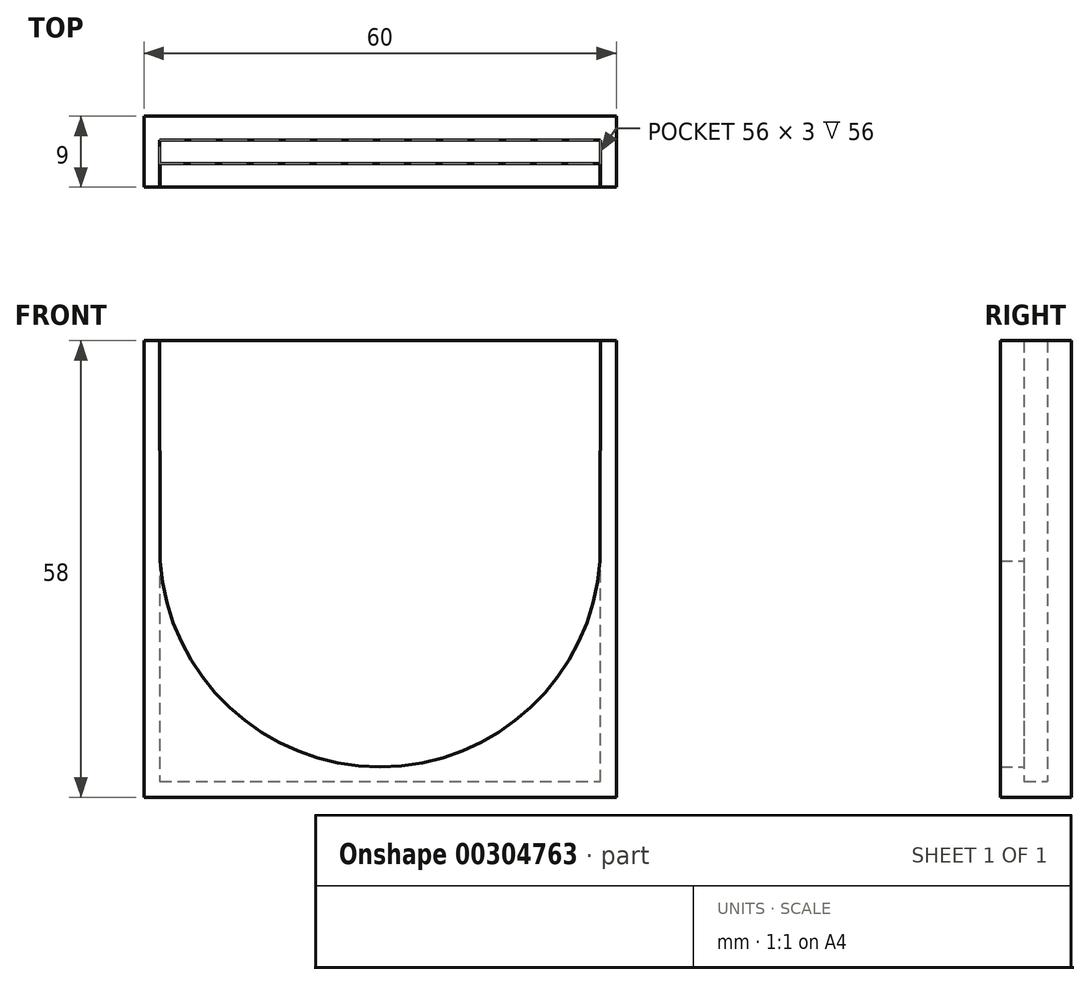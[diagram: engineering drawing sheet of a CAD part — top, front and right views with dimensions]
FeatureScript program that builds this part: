
annotation { "Feature Type Name" : "Feature", "Feature Type Description" : "" }
export const myFeature = defineFeature(function(context is Context, id is Id, definition is map)
    precondition{}
    {
        {
            var Q0;
            Q0=qCreatedBy(makeId("Front.planeOp"),FACE);
            var sketch = newSketch(context, id + "F0", { "sketchPlane" : qUnion([Q0])});
            skLineSegment(sketch, "E0.bottom", {"start": v(30, -30) * mm, "end": v(-30, -30) * mm});
            skLineSegment(sketch, "E0.top", {"start": v(30, 30) * mm, "end": v(-30, 30) * mm});
            skLineSegment(sketch, "E0.left", {"start": v(30, -30) * mm, "end": v(30, 30) * mm});
            skLineSegment(sketch, "E0.right", {"start": v(-30, -30) * mm, "end": v(-30, 30) * mm});
            skPoint(sketch, "E0.middle", {"position": v(0, 0) * mm});
            skLineSegment(sketch, "E1", {"start": v(-30, 28) * mm, "end": v(30, 28) * mm});
            skSolve(sketch);
        }
        {
            var Q0;
            Q0=makeQuery(id+"F0.imprint","IMPRINT",FACE,{"disambiguationData":[TD([[makeQuery(id+"F0.imprint","IMPRINT",EDGE,{"derivedFrom":sQuery(id+"F0.wireOp",EDGE,"E0.bottom")}),-1.0]])]});
            extrude(context, id + "F1", {"entities" : qUnion([Q0]), "oppositeDirection" : true, "depth" : 3 * mm});
        }
        {
            var Q0;
            Q0=makeQuery(id+"F1.opExtrude","CAP_FACE",FACE,{"disambiguationData":[OSD([sQuery(id+"F0.wireOp",EDGE,"E0.bottom"),sQuery(id+"F0.wireOp",EDGE,"E0.top"),sQuery(id+"F0.wireOp",EDGE,"E0.left"),sQuery(id+"F0.wireOp",EDGE,"E0.right")])],"isStart":true});
            var sketch = newSketch(context, id + "F2", { "sketchPlane" : qUnion([Q0])});
            skSolve(sketch);
        }
        {
            var Q0;
            Q0=makeQuery(id+"F2.imprint","IMPRINT",FACE,{"disambiguationData":[TD([[makeQuery(id+"F2.imprint","IMPRINT",EDGE,{"derivedFrom":makeQuery(id+"F1.opExtrude","CAP_EDGE",EDGE,{"disambiguationData":[OSD([sQuery(id+"F0.wireOp",EDGE,"E0.bottom")])],"isStart":true})}),-1.0]])]});
            var sketch = newSketch(context, id + "F3", { "sketchPlane" : qUnion([Q0])});
            skLineSegment(sketch, "E2.0", {"start": v(-28, -28) * mm, "end": v(28, -28) * mm});
            skLineSegment(sketch, "E2.1", {"start": v(-28, 28) * mm, "end": v(-28, -28) * mm});
            skLineSegment(sketch, "E2.3", {"start": v(28, -28) * mm, "end": v(28, 28) * mm});
            skLineSegment(sketch, "E3", {"start": v(-28, 28) * mm, "end": v(-30, 28) * mm});
            skLineSegment(sketch, "E4", {"start": v(-30, 28) * mm, "end": v(-30, -30) * mm});
            skLineSegment(sketch, "E5", {"start": v(-30, -30) * mm, "end": v(30, -30) * mm});
            skLineSegment(sketch, "E6", {"start": v(30, -30) * mm, "end": v(30, 28) * mm});
            skLineSegment(sketch, "E7", {"start": v(30, 28) * mm, "end": v(28, 28) * mm});
            skSolve(sketch);
        }
        {
            var Q0;
            Q0 = qSketchRegion(id + "F3", true);
            extrude(context, id + "F4", {"entities" : qUnion([Q0]), "operationType" : NewBodyOperationType.ADD, "depth" : 3 * mm});
        }
        {
            var Q0;
            Q0=makeQuery(id+"F4.opExtrude","CAP_FACE",FACE,{"disambiguationData":[OSD([sQuery(id+"F3.wireOp",EDGE,"E2.0"),sQuery(id+"F3.wireOp",EDGE,"E2.1"),sQuery(id+"F3.wireOp",EDGE,"E2.3"),sQuery(id+"F3.wireOp",EDGE,"E3"),sQuery(id+"F3.wireOp",EDGE,"E4"),sQuery(id+"F3.wireOp",EDGE,"E5"),sQuery(id+"F3.wireOp",EDGE,"E6"),sQuery(id+"F3.wireOp",EDGE,"E7")])],"isStart":false});
            var sketch = newSketch(context, id + "F5", { "sketchPlane" : qUnion([Q0])});
            skLineSegment(sketch, "E8.bottom", {"start": v(-30, -30) * mm, "end": v(30, -30) * mm});
            skLineSegment(sketch, "E8.top", {"start": v(-30, 28) * mm, "end": v(-28, 28) * mm});
            skLineSegment(sketch, "E8.left", {"start": v(-30, -30) * mm, "end": v(-30, 28) * mm});
            skLineSegment(sketch, "E8.right", {"start": v(30, -30) * mm, "end": v(30, 28) * mm});
            skArc(sketch, "E9", {"start": v(-27.95, 3.6) * mm, "mid": v(0, -26.14) * mm, "end": v(27.95, 3.6) * mm});
            skLineSegment(sketch, "E10", {"start": v(28, 28) * mm, "end": v(27.94, 0) * mm});
            skLineSegment(sketch, "E11", {"start": v(-28, 28) * mm, "end": v(-27.94, 0) * mm});
            skLineSegment(sketch, "E12.trimOffspring", {"start": v(28, 28) * mm, "end": v(30, 28) * mm});
            skSolve(sketch);
        }
        {
            var Q0;
            Q0 = qSketchRegion(id + "F5", true);
            extrude(context, id + "F6", {"entities" : qUnion([Q0]), "operationType" : NewBodyOperationType.ADD, "depth" : 3 * mm});
        }
    });
